# Revit family: ST eco Dl Flat & SylFlat _ SUR
name_source: partatom
category: Lighting Fixtures
revit_build: Autodesk Revit 2017 (Build: 20190507_1515(x64)
units: mm (PartAtom-declared; Revit-internal decimal feet)

## family parameters
Cut with Voids When Loaded = No
Host = Face
Light Source = Yes
OmniClass Number = 23.80.70.00
OmniClass Title = Lighting
Part Type = Normal
Room Calculation Point = No
Round Connector Dimension = Use Diameter
Shared = No

## types (4) — shared parameters
Assembly Code = D5020200
AssetType = Fixed
CHAMF_2_SYL = 1 mm  [stored 0.00328084 ft]
CHAMF_SYL = 1 mm  [stored 0.00328084 ft]
CLIP_CUTOUT_SYL = 19 mm  [stored 0.062336 ft]
CLIP_HOLE_HE_SYL = 9 mm  [stored 0.0295276 ft]
CLIP_HOLE_SYL = 3 mm  [stored 0.00984252 ft]
CLIP_SYL = 10 mm  [stored 0.0328084 ft]
ClassificationName = Uniclass2015
ClassificationValue = EF_70_80
Color Filter = 16777215
Default Elevation = 1219 mm
Dimming Lamp Color Temperature Shift = <None>
DocumentationLiterature = http://www.sylvania-lighting.com
ElectricShockClassification = Class II
Emit Shape Visible in Rendering = No
Emit from Circle Diameter = 610 mm
IfcExportAs = IfcLightFixtureType
IfcExportType = IfcLightFixtureType
ImpactProtectionIndex = IK06
IngressProtection = IP20
Keynote = 16500
LUM_HEIGHT_SYL = 14 mm  [stored 0.0459318 ft]
LUM_MH_SYL = 37 mm
Lamp = LED
LampColourRenderingIndex = 80
LampMacAdamStep = 5
LampsType = LED
Manufacturer = Feilo Sylvania
ManufacturerName = Feilo Sylvania
Material_1_SYL = <By Category>
Material_2_SYL = <By Category>
Material_3_SYL = <By Category>
Material_4_SYL = <By Category>
NominalHeight = 38 mm  [stored 0.124672 ft]
PowerFactor = 0.9
Tilt Angle = -90.00°
Type Image = <None>
URL = http://www.sylvania-lighting.com
Voltage = 0 V
zero-valued in all types: Cost

## per-type parameters (varying)
| type | Apparent Load | CLIP_DIST_SYL | CLIP_D_SYL | Description | LampColourTemperature | LampNominalLuminous | LuminousEfficacy | Material | Model | ModelNumber | ModelReference | Name | NominalDepth | NominalLength | Photometric Web File | PowerConsumption | R1_SYL | R2_SYL | R_DIFF_SYL | SIZE_155_SYL | SIZE_203_SYL | TypeName | Weight |
| 0053947 ST E DOWNLIGHT FLT 172 1200 840 DIM SRFC | 12 VA | 75 mm  [stored 0.246063 ft] | 75 mm  [stored 0.246063 ft] | START eco Downlight Flat DIM Surface is an integrated LED surface mounted downlight with separated phase dimmable driver; 12W; 1200Lm; 100Lm/W; 4000K; IP20; 30,000hrs (L70B50). | 4000 K | 1200 lm | 100 lm/W | aluminium housing, other diffuser | START eco Downlight Flat 172 1200lm 840 DIM Srfc | 0053947 | START eco Downlight Flat 172 1200lm 840 DIM Srfc | START eco Downlight Flat 172 1200lm 840 DIM Srfc | 172 mm  [stored 0.564304 ft] | 172 mm  [stored 0.564304 ft] | 0053947.ies | 12 W | 86 mm  [stored 0.282152 ft] | 78 mm | 63 mm | 1 | 0 | START eco Downlight Flat 172 1200lm 840 DIM Srfc | 4.87 kg |
| 0053946 ST E DOWNLIGHT FLT 226 1700 830 DIM SRFC | 17 VA | 99 mm  [stored 0.324803 ft] | 99 mm  [stored 0.324803 ft] | START eco Downlight Flat DIM Surface is an integrated LED surface mounted downlight with separated phase dimmable driver; 17W; 1700Lm; 100Lm/W; 3000K; IP20; 30,000hrs (L70B50). | 3000 K | 1700 lm | 100 lm/W |  | START eco Downlight Flat 226 1700lm 830 DIM Srfc | 0053946 | START eco Downlight Flat 226 1700lm 830 DIM Srfc | START eco Downlight Flat 226 1700lm 830 DIM Srfc | 226 mm  [stored 0.74147 ft] | 226 mm  [stored 0.74147 ft] | 0053946.ies | 17 W | 113 mm  [stored 0.370735 ft] | 102 mm | 88 mm  [stored 0.288714 ft] | 0 | 1 | START eco Downlight Flat 226 1700lm 830 DIM Srfc | 6.87 kg |
| 0053945 ST E DOWNLIGHT FLT 172 1100 830 DIM SRFC | 12 VA | 75 mm  [stored 0.246063 ft] | 75 mm  [stored 0.246063 ft] | START eco Downlight Flat DIM Surface is an integrated LED surface mounted downlight with separated phase dimmable driver; 12W; 1100Lm; 92Lm/W; 3000K; IP20; 30,000hrs (L70B50). | 3000 K | 1100 lm | 92 lm/W | aluminium housing, other diffuser | START eco Downlight Flat 172 1100lm 830 DIM Srfc | 0053945 | START eco Downlight Flat 172 1100lm 830 DIM Srfc | START eco Downlight Flat 172 1100lm 830 DIM Srfc | 172 mm  [stored 0.564304 ft] | 172 mm  [stored 0.564304 ft] | 0053945.ies | 12 W | 86 mm  [stored 0.282152 ft] | 78 mm | 63 mm | 1 | 0 | START eco Downlight Flat 172 1100lm 830 DIM Srfc | 4.87 kg |
| 0053948 ST E DOWNLIGHT FLT 226 1750 840 DIM SRFC | 17 VA | 99 mm  [stored 0.324803 ft] | 99 mm  [stored 0.324803 ft] | START eco Downlight Flat DIM Surface is an integrated LED surface mounted downlight with separated phase dimmable driver; 17W; 1750Lm; 103Lm/W; 4000K; IP20; 30,000hrs (L70B50). | 4000 K | 1750 lm | 103 lm/W |  | START eco Downlight Flat 226 1750lm 840 DIM Srfc | 0053948 | START eco Downlight Flat 226 1750lm 840 DIM Srfc | START eco Downlight Flat 226 1750lm 840 DIM Srfc | 226 mm  [stored 0.74147 ft] | 226 mm  [stored 0.74147 ft] | 0053948.ies | 17 W | 113 mm  [stored 0.370735 ft] | 102 mm | 88 mm  [stored 0.288714 ft] | 0 | 1 | START eco Downlight Flat 226 1750lm 840 DIM Srfc | 6.87 kg |

note: [stored X ft] marks values corroborated as IEEE doubles in the binary element streams (Revit-internal decimal feet)

## geometry (parser evidence)
native form markers: Sweep x3
no freeform markers — native parametric forms only
